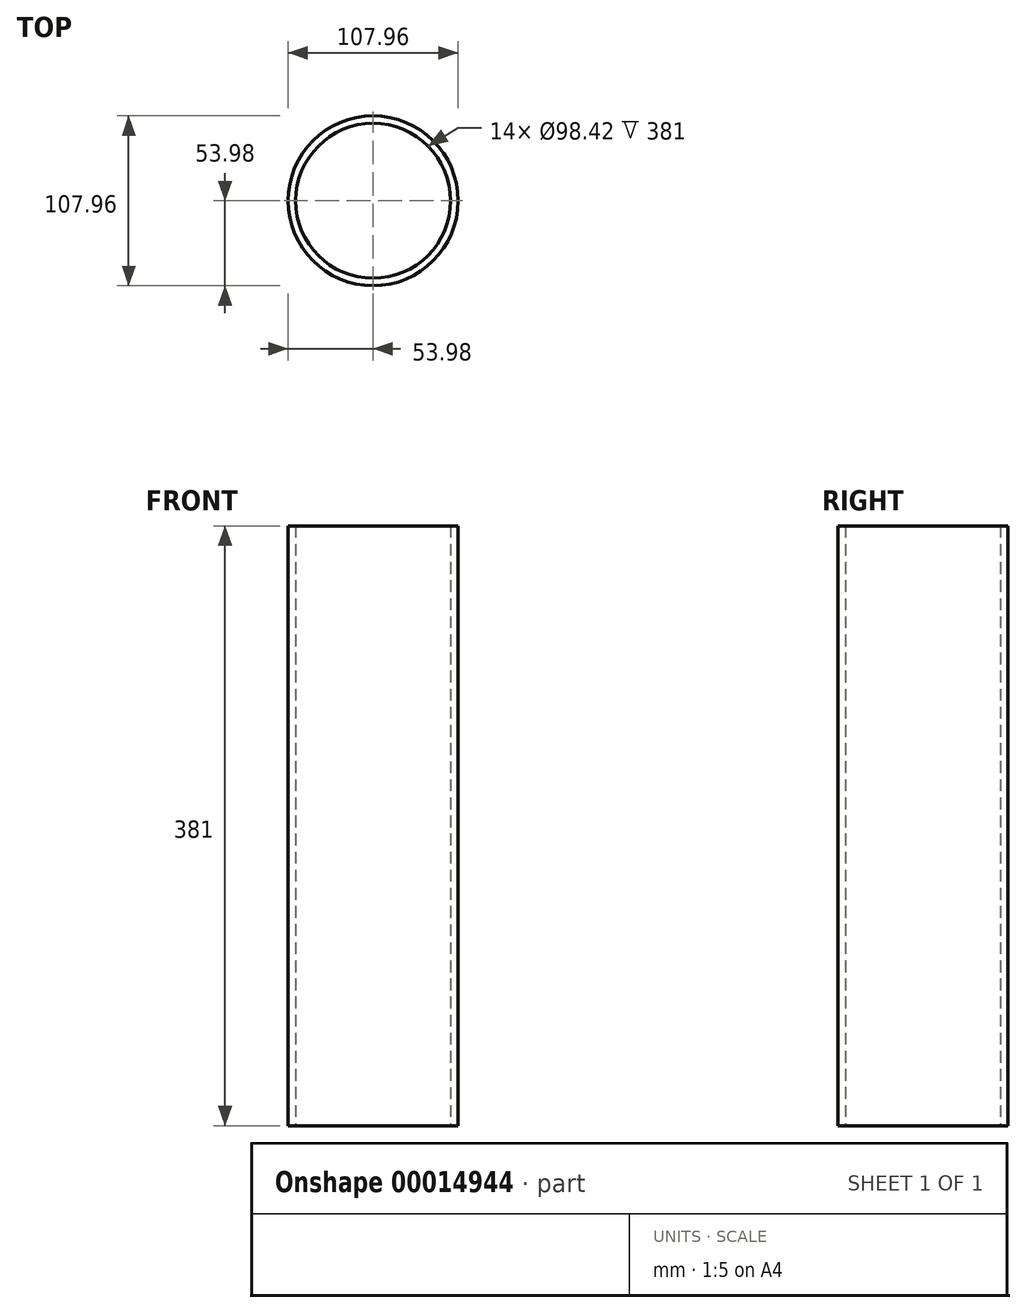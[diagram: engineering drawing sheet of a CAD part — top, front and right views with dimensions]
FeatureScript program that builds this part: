
annotation { "Feature Type Name" : "Feature", "Feature Type Description" : "" }
export const myFeature = defineFeature(function(context is Context, id is Id, definition is map)
    precondition{}
    {
        {
            var Q0;
            Q0=qCreatedBy(makeId("Top.planeOp"),FACE);
            var sketch = newSketch(context, id + "F0", { "sketchPlane" : qUnion([Q0])});
            skCircle(sketch, "E0", {"center": v(0, 0) * mm, "radius": 49.21 * mm});
            skCircle(sketch, "E1", {"center": v(0, 0) * mm, "radius": 53.98 * mm});
            skSolve(sketch);
        }
        {
            var Q0;
            Q0=makeQuery(id+"F0.imprint","IMPRINT",FACE,{"disambiguationData":[TD([[makeQuery(id+"F0.imprint","IMPRINT",EDGE,{"derivedFrom":sQuery(id+"F0.wireOp",EDGE,"E0")}),-1.0]])]});
            extrude(context, id + "F1", {"entities" : qUnion([Q0]), "depth" : 381 * mm});
        }
    });
